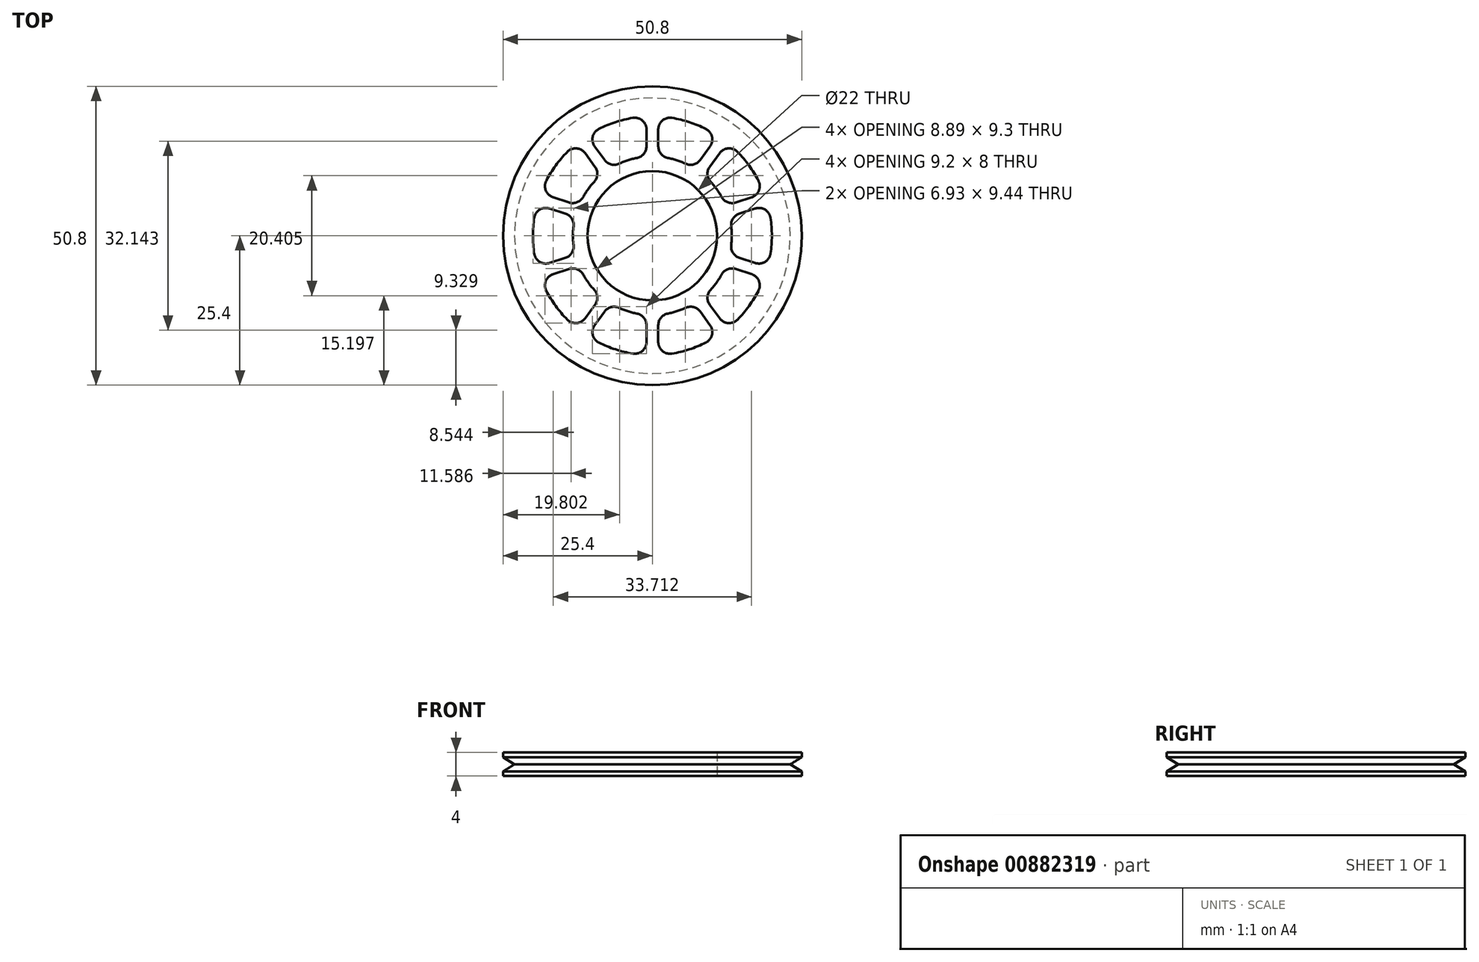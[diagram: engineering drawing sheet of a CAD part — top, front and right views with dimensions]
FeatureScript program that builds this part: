
annotation { "Feature Type Name" : "Feature", "Feature Type Description" : "" }
export const myFeature = defineFeature(function(context is Context, id is Id, definition is map)
    precondition{}
    {
        {
            var Q0;
            Q0=qCreatedBy(makeId("Top.planeOp"),FACE);
            var sketch = newSketch(context, id + "F0", { "sketchPlane" : qUnion([Q0])});
            skCircle(sketch, "E0", {"center": v(0, 0) * mm, "radius": 25.4 * mm});
            skCircle(sketch, "E1", {"center": v(0, 0) * mm, "radius": 11 * mm});
            skArc(sketch, "E2.0", {"start": v(-3.33, 20.05) * mm, "mid": v(-6.28, 19.33) * mm, "end": v(-9.1, 18.17) * mm});
            skArc(sketch, "E3.0", {"start": v(-2.61, 13.24) * mm, "mid": v(-4.17, 12.84) * mm, "end": v(-5.67, 12.25) * mm});
            skLineSegment(sketch, "E4.0", {"start": v(1, 18.07) * mm, "end": v(1, 15.2) * mm});
            skLineSegment(sketch, "E5.0", {"start": v(-1, 18.07) * mm, "end": v(-1, 15.2) * mm});
            skPoint(sketch, "E6.orphan", {"position": v(0, 22.98) * mm});
            skPoint(sketch, "E7.visualSharp", {"position": v(-1, 20.3) * mm});
            skArc(sketch, "E7.filletArc", {"start": v(-1, 18.07) * mm, "mid": v(-1.7, 19.6) * mm, "end": v(-3.33, 20.05) * mm});
            skPoint(sketch, "E8.visualSharp", {"position": v(1, 20.3) * mm});
            skArc(sketch, "E8.filletArc", {"start": v(3.33, 20.05) * mm, "mid": v(1.7, 19.6) * mm, "end": v(1, 18.07) * mm});
            skPoint(sketch, "E9.visualSharp", {"position": v(-1, 13.46) * mm});
            skArc(sketch, "E9.filletArc", {"start": v(-2.61, 13.24) * mm, "mid": v(-1.45, 13.94) * mm, "end": v(-1, 15.2) * mm});
            skPoint(sketch, "E10.visualSharp", {"position": v(1, 13.46) * mm});
            skArc(sketch, "E10.filletArc", {"start": v(1, 15.2) * mm, "mid": v(1.45, 13.94) * mm, "end": v(2.61, 13.24) * mm});
            skArc(sketch, "E11.1.0", {"start": v(-11.43, 14.03) * mm, "mid": v(-12.9, 14.85) * mm, "end": v(-14.47, 14.26) * mm});
            skArc(sketch, "E11.1.1", {"start": v(-9.1, 18.17) * mm, "mid": v(-10.14, 16.86) * mm, "end": v(-9.81, 15.2) * mm});
            skLineSegment(sketch, "E11.1.2", {"start": v(-9.81, 15.2) * mm, "end": v(-8.13, 12.9) * mm});
            skLineSegment(sketch, "E11.1.3", {"start": v(-11.43, 14.03) * mm, "end": v(-9.75, 11.71) * mm});
            skArc(sketch, "E11.1.4", {"start": v(-9.9, 9.18) * mm, "mid": v(-9.37, 10.42) * mm, "end": v(-9.75, 11.71) * mm});
            skArc(sketch, "E11.1.5", {"start": v(-8.13, 12.9) * mm, "mid": v(-7.01, 12.13) * mm, "end": v(-5.67, 12.25) * mm});
            skArc(sketch, "E11.2.0", {"start": v(-17.5, 4.63) * mm, "mid": v(-19.17, 4.43) * mm, "end": v(-20.1, 3.03) * mm});
            skArc(sketch, "E11.2.1", {"start": v(-18.04, 9.36) * mm, "mid": v(-18.11, 7.68) * mm, "end": v(-16.88, 6.54) * mm});
            skLineSegment(sketch, "E11.2.2", {"start": v(-16.88, 6.54) * mm, "end": v(-14.15, 5.65) * mm});
            skLineSegment(sketch, "E11.2.3", {"start": v(-17.5, 4.63) * mm, "end": v(-14.77, 3.75) * mm});
            skArc(sketch, "E11.2.4", {"start": v(-13.4, 1.6) * mm, "mid": v(-13.7, 2.92) * mm, "end": v(-14.77, 3.75) * mm});
            skArc(sketch, "E11.2.5", {"start": v(-14.15, 5.65) * mm, "mid": v(-12.8, 5.7) * mm, "end": v(-11.79, 6.58) * mm});
            skArc(sketch, "E11.3.0", {"start": v(-16.88, -6.54) * mm, "mid": v(-18.11, -7.68) * mm, "end": v(-18.04, -9.36) * mm});
            skArc(sketch, "E11.3.1", {"start": v(-20.1, -3.03) * mm, "mid": v(-19.17, -4.43) * mm, "end": v(-17.5, -4.63) * mm});
            skLineSegment(sketch, "E11.3.2", {"start": v(-17.5, -4.63) * mm, "end": v(-14.77, -3.75) * mm});
            skLineSegment(sketch, "E11.3.3", {"start": v(-16.88, -6.54) * mm, "end": v(-14.15, -5.65) * mm});
            skArc(sketch, "E11.3.4", {"start": v(-11.79, -6.58) * mm, "mid": v(-12.8, -5.7) * mm, "end": v(-14.15, -5.65) * mm});
            skArc(sketch, "E11.3.5", {"start": v(-14.77, -3.75) * mm, "mid": v(-13.7, -2.92) * mm, "end": v(-13.4, -1.6) * mm});
            skArc(sketch, "E11.4.0", {"start": v(-9.81, -15.2) * mm, "mid": v(-10.14, -16.86) * mm, "end": v(-9.1, -18.17) * mm});
            skArc(sketch, "E11.4.1", {"start": v(-14.47, -14.26) * mm, "mid": v(-12.9, -14.85) * mm, "end": v(-11.43, -14.03) * mm});
            skLineSegment(sketch, "E11.4.2", {"start": v(-11.43, -14.03) * mm, "end": v(-9.75, -11.71) * mm});
            skLineSegment(sketch, "E11.4.3", {"start": v(-9.81, -15.2) * mm, "end": v(-8.13, -12.9) * mm});
            skArc(sketch, "E11.4.4", {"start": v(-5.67, -12.25) * mm, "mid": v(-7.01, -12.13) * mm, "end": v(-8.13, -12.9) * mm});
            skArc(sketch, "E11.4.5", {"start": v(-9.75, -11.71) * mm, "mid": v(-9.37, -10.42) * mm, "end": v(-9.9, -9.18) * mm});
            skArc(sketch, "E11.5.0", {"start": v(1, -18.07) * mm, "mid": v(1.7, -19.6) * mm, "end": v(3.33, -20.05) * mm});
            skArc(sketch, "E11.5.1", {"start": v(-3.33, -20.05) * mm, "mid": v(-1.7, -19.6) * mm, "end": v(-1, -18.07) * mm});
            skLineSegment(sketch, "E11.5.2", {"start": v(-1, -18.07) * mm, "end": v(-1, -15.2) * mm});
            skLineSegment(sketch, "E11.5.3", {"start": v(1, -18.07) * mm, "end": v(1, -15.2) * mm});
            skArc(sketch, "E11.5.4", {"start": v(2.61, -13.24) * mm, "mid": v(1.45, -13.94) * mm, "end": v(1, -15.2) * mm});
            skArc(sketch, "E11.5.5", {"start": v(-1, -15.2) * mm, "mid": v(-1.45, -13.94) * mm, "end": v(-2.61, -13.24) * mm});
            skArc(sketch, "E11.6.0", {"start": v(11.43, -14.03) * mm, "mid": v(12.9, -14.85) * mm, "end": v(14.47, -14.26) * mm});
            skArc(sketch, "E11.6.1", {"start": v(9.1, -18.17) * mm, "mid": v(10.14, -16.86) * mm, "end": v(9.81, -15.2) * mm});
            skLineSegment(sketch, "E11.6.2", {"start": v(9.81, -15.2) * mm, "end": v(8.13, -12.9) * mm});
            skLineSegment(sketch, "E11.6.3", {"start": v(11.43, -14.03) * mm, "end": v(9.75, -11.71) * mm});
            skArc(sketch, "E11.6.4", {"start": v(9.9, -9.18) * mm, "mid": v(9.37, -10.42) * mm, "end": v(9.75, -11.71) * mm});
            skArc(sketch, "E11.6.5", {"start": v(8.13, -12.9) * mm, "mid": v(7.01, -12.13) * mm, "end": v(5.67, -12.25) * mm});
            skArc(sketch, "E11.7.0", {"start": v(17.5, -4.63) * mm, "mid": v(19.17, -4.43) * mm, "end": v(20.1, -3.03) * mm});
            skArc(sketch, "E11.7.1", {"start": v(18.04, -9.36) * mm, "mid": v(18.11, -7.68) * mm, "end": v(16.88, -6.54) * mm});
            skLineSegment(sketch, "E11.7.2", {"start": v(16.88, -6.54) * mm, "end": v(14.15, -5.65) * mm});
            skLineSegment(sketch, "E11.7.3", {"start": v(17.5, -4.63) * mm, "end": v(14.77, -3.75) * mm});
            skArc(sketch, "E11.7.4", {"start": v(13.4, -1.6) * mm, "mid": v(13.7, -2.92) * mm, "end": v(14.77, -3.75) * mm});
            skArc(sketch, "E11.7.5", {"start": v(14.15, -5.65) * mm, "mid": v(12.8, -5.7) * mm, "end": v(11.79, -6.58) * mm});
            skArc(sketch, "E12.trimOffspring", {"start": v(-14.47, 14.26) * mm, "mid": v(-16.44, 11.94) * mm, "end": v(-18.04, 9.36) * mm});
            skArc(sketch, "E13.trimOffspring", {"start": v(-9.9, 9.18) * mm, "mid": v(-10.92, 7.94) * mm, "end": v(-11.79, 6.58) * mm});
            skArc(sketch, "E14.trimOffspring", {"start": v(-13.4, 1.6) * mm, "mid": v(-13.5, 0) * mm, "end": v(-13.4, -1.6) * mm});
            skArc(sketch, "E15.trimOffspring", {"start": v(-20.1, 3.03) * mm, "mid": v(-20.32, 0) * mm, "end": v(-20.1, -3.03) * mm});
            skArc(sketch, "E16.trimOffspring", {"start": v(-18.04, -9.36) * mm, "mid": v(-16.44, -11.94) * mm, "end": v(-14.47, -14.26) * mm});
            skArc(sketch, "E17.trimOffspring", {"start": v(-11.79, -6.58) * mm, "mid": v(-10.92, -7.94) * mm, "end": v(-9.9, -9.18) * mm});
            skArc(sketch, "E18.trimOffspring", {"start": v(-5.67, -12.25) * mm, "mid": v(-4.17, -12.84) * mm, "end": v(-2.61, -13.24) * mm});
            skArc(sketch, "E19.trimOffspring", {"start": v(-9.1, -18.17) * mm, "mid": v(-6.28, -19.33) * mm, "end": v(-3.33, -20.05) * mm});
            skArc(sketch, "E20.trimOffspring", {"start": v(3.33, -20.05) * mm, "mid": v(6.28, -19.33) * mm, "end": v(9.1, -18.17) * mm});
            skArc(sketch, "E21.trimOffspring", {"start": v(2.61, -13.24) * mm, "mid": v(4.17, -12.84) * mm, "end": v(5.67, -12.25) * mm});
            skArc(sketch, "E22.trimOffspring", {"start": v(9.9, -9.18) * mm, "mid": v(10.92, -7.94) * mm, "end": v(11.79, -6.58) * mm});
            skArc(sketch, "E23.trimOffspring", {"start": v(14.47, -14.26) * mm, "mid": v(16.44, -11.94) * mm, "end": v(18.04, -9.36) * mm});
            skArc(sketch, "E24.trimOffspring", {"start": v(9.1, 18.17) * mm, "mid": v(6.28, 19.33) * mm, "end": v(3.33, 20.05) * mm});
            skArc(sketch, "E25.trimOffspring", {"start": v(5.67, 12.25) * mm, "mid": v(4.17, 12.84) * mm, "end": v(2.61, 13.24) * mm});
            skArc(sketch, "E26.1.8.0", {"start": v(16.88, 6.54) * mm, "mid": v(18.11, 7.68) * mm, "end": v(18.04, 9.36) * mm});
            skArc(sketch, "E26.4.8.0", {"start": v(20.1, 3.03) * mm, "mid": v(19.17, 4.43) * mm, "end": v(17.5, 4.63) * mm});
            skLineSegment(sketch, "E26.8.8.0", {"start": v(17.5, 4.63) * mm, "end": v(14.77, 3.75) * mm});
            skLineSegment(sketch, "E26.11.8.0", {"start": v(16.88, 6.54) * mm, "end": v(14.15, 5.65) * mm});
            skArc(sketch, "E26.14.8.0", {"start": v(11.79, 6.58) * mm, "mid": v(12.8, 5.7) * mm, "end": v(14.15, 5.65) * mm});
            skArc(sketch, "E26.18.8.0", {"start": v(14.77, 3.75) * mm, "mid": v(13.7, 2.92) * mm, "end": v(13.4, 1.6) * mm});
            skArc(sketch, "E26.1.9.0", {"start": v(9.81, 15.2) * mm, "mid": v(10.14, 16.86) * mm, "end": v(9.1, 18.17) * mm});
            skArc(sketch, "E26.4.9.0", {"start": v(14.47, 14.26) * mm, "mid": v(12.9, 14.85) * mm, "end": v(11.43, 14.03) * mm});
            skLineSegment(sketch, "E26.8.9.0", {"start": v(11.43, 14.03) * mm, "end": v(9.75, 11.71) * mm});
            skLineSegment(sketch, "E26.11.9.0", {"start": v(9.81, 15.2) * mm, "end": v(8.13, 12.9) * mm});
            skArc(sketch, "E26.14.9.0", {"start": v(5.67, 12.25) * mm, "mid": v(7.01, 12.13) * mm, "end": v(8.13, 12.9) * mm});
            skArc(sketch, "E26.18.9.0", {"start": v(9.75, 11.71) * mm, "mid": v(9.37, 10.42) * mm, "end": v(9.9, 9.18) * mm});
            skArc(sketch, "E27.trimOffspring", {"start": v(18.04, 9.36) * mm, "mid": v(16.44, 11.94) * mm, "end": v(14.47, 14.26) * mm});
            skArc(sketch, "E28.trimOffspring", {"start": v(11.79, 6.58) * mm, "mid": v(10.92, 7.94) * mm, "end": v(9.9, 9.18) * mm});
            skArc(sketch, "E29.trimOffspring", {"start": v(13.4, -1.6) * mm, "mid": v(13.5, 0) * mm, "end": v(13.4, 1.6) * mm});
            skArc(sketch, "E30.trimOffspring", {"start": v(20.1, -3.03) * mm, "mid": v(20.32, 0) * mm, "end": v(20.1, 3.03) * mm});
            skSolve(sketch);
        }
        {
            var Q0;
            Q0=makeQuery(id+"F0.imprint","IMPRINT",FACE,{"disambiguationData":[TD([[makeQuery(id+"F0.imprint","IMPRINT",EDGE,{"derivedFrom":sQuery(id+"F0.wireOp",EDGE,"E0")}),1.0]])]});
            extrude(context, id + "F1", {"entities" : qUnion([Q0]), "endBound" : BoundingType.SYMMETRIC, "depth" : 4 * mm, "offsetDistance" : 25.4 * mm});
        }
        {
            var Q0;
            Q0=qCreatedBy(makeId("Right.planeOp"),FACE);
            var sketch = newSketch(context, id + "F2", { "sketchPlane" : qUnion([Q0])});
            skLineSegment(sketch, "E31", {"start": v(-25.44, 0) * mm, "end": v(-23.44, 0) * mm});
            skLineSegment(sketch, "E32", {"start": v(-23.44, 0) * mm, "end": v(-25.44, 1.24) * mm});
            skLineSegment(sketch, "E33", {"start": v(-25.44, 1.24) * mm, "end": v(-25.44, 0) * mm});
            skLineSegment(sketch, "E34.MirrorCS", {"start": v(-23.44, 0) * mm, "end": v(-25.44, -1.24) * mm});
            skLineSegment(sketch, "E35.MirrorCS", {"start": v(-25.44, -1.24) * mm, "end": v(-25.44, 0) * mm});
            skPoint(sketch, "E36.start.orphan", {"position": v(0, 11.59) * mm});
            skLineSegment(sketch, "E37", {"start": v(0, -23.6) * mm, "end": v(0, 11.59) * mm, "construction": true});
            skSolve(sketch);
        }
        {
            var Q0;
            Q0 = qSketchRegion(id + "F2", true);
            var Q1;
            Q1=sQuery(id+"F2.wireOp",EDGE,"E37");
            revolve(context, id + "F3", {"operationType" : NewBodyOperationType.REMOVE, "surfaceOperationType" : NewSurfaceOperationType.NEW, "entities" : qUnion([Q0]), "axis" : qUnion([Q1]), "revolveType" : RevolveType.FULL, "oppositeDirection" : true});
        }
    });
